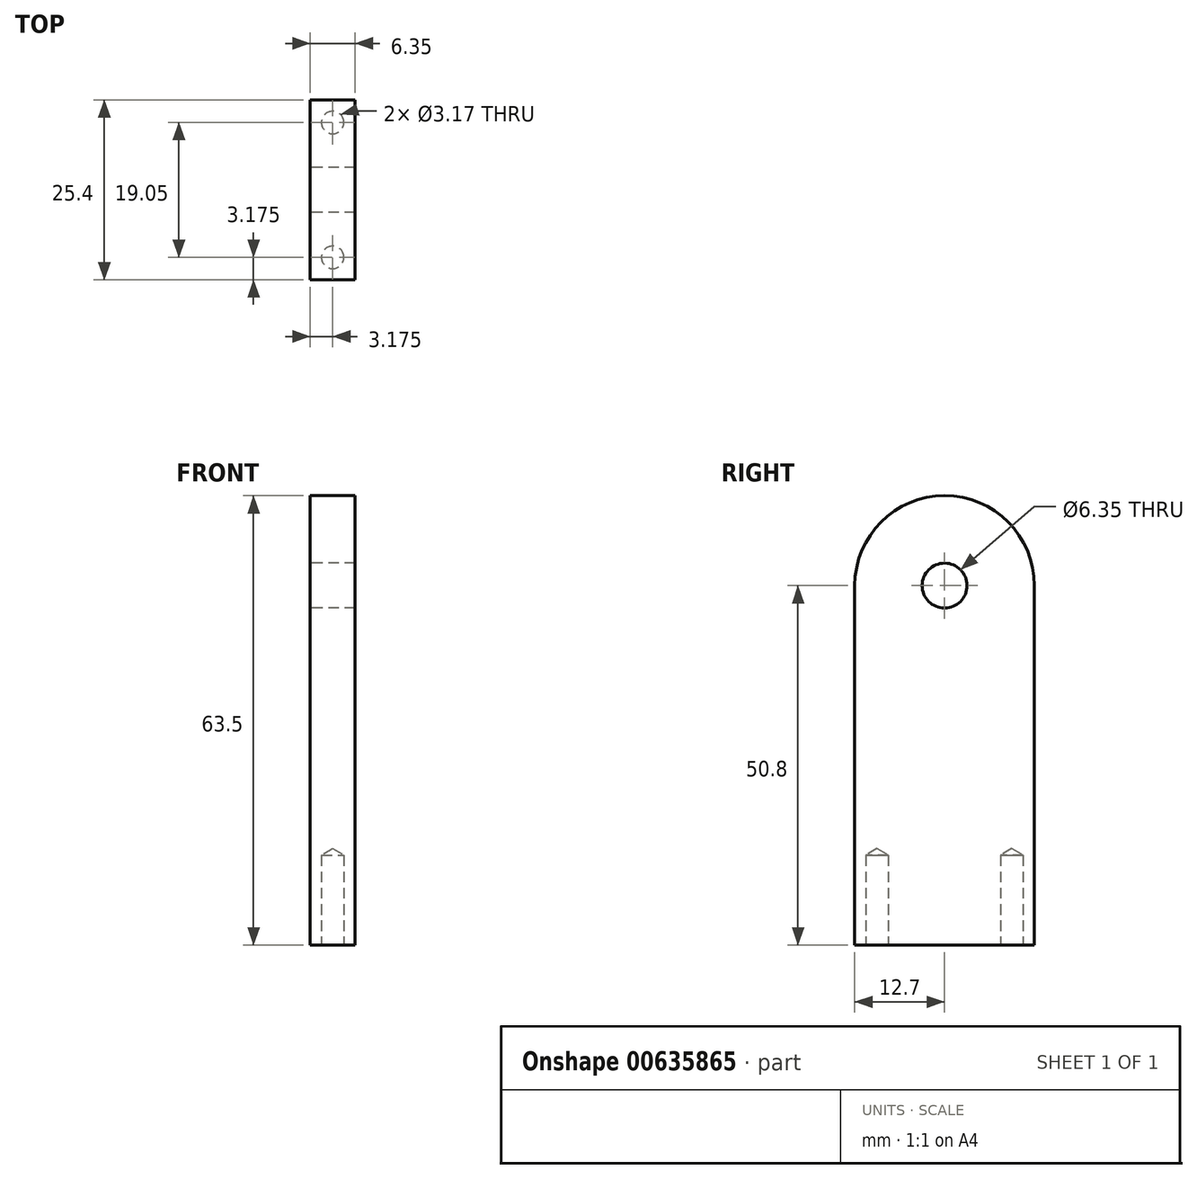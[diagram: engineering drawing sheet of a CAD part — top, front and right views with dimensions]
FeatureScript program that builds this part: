
annotation { "Feature Type Name" : "Feature", "Feature Type Description" : "" }
export const myFeature = defineFeature(function(context is Context, id is Id, definition is map)
    precondition{}
    {
        {
            var Q0;
            Q0=qCreatedBy(makeId("Right.planeOp"),FACE);
            var sketch = newSketch(context, id + "F0", { "sketchPlane" : qUnion([Q0])});
            skLineSegment(sketch, "E0.bottom", {"start": v(0, 0) * mm, "end": v(25.4, 0) * mm});
            skLineSegment(sketch, "E0.top", {"start": v(0, 50.8) * mm, "end": v(25.4, 50.8) * mm});
            skLineSegment(sketch, "E0.left", {"start": v(0, 0) * mm, "end": v(0, 50.8) * mm});
            skLineSegment(sketch, "E0.right", {"start": v(25.4, 0) * mm, "end": v(25.4, 50.8) * mm});
            skCircle(sketch, "E1", {"center": v(12.7, 50.8) * mm, "radius": 12.7 * mm});
            skCircle(sketch, "E2", {"center": v(12.7, 50.8) * mm, "radius": 3.18 * mm});
            skSolve(sketch);
        }
        {
            var Q0;
            Q0=makeQuery(id+"F0.imprint","IMPRINT",FACE,{"disambiguationData":[TD([[makeQuery(id+"F0.imprint","IMPRINT",EDGE,{"derivedFrom":sQuery(id+"F0.wireOp",EDGE,"E0.bottom")}),1.0]])]});
            var Q1;
            {var subQ1=sQuery(id+"F0.wireOp",EDGE,"E0.top");var subQ3=sQuery(id+"F0.wireOp",EDGE,"E2");var subQ4=makeQuery(id+"F0.imprint","INTERSECT",VERTEX,{"disambiguationData":[OD(0.0)],"derivedFrom":[subQ1,subQ3]});Q1=makeQuery(id+"F0.imprint","IMPRINT",FACE,{"disambiguationData":[TD([[makeQuery(id+"F0.imprint","IMPRINT",EDGE,{"disambiguationData":[TD([[subQ4,-1.0]])],"derivedFrom":subQ3}),-1.0]])]});}
            var Q2;
            {var subQ1=sQuery(id+"F0.wireOp",EDGE,"E0.top");var subQ3=sQuery(id+"F0.wireOp",EDGE,"E2");var subQ4=makeQuery(id+"F0.imprint","INTERSECT",VERTEX,{"disambiguationData":[OD(0.0)],"derivedFrom":[subQ1,subQ3]});Q2=makeQuery(id+"F0.imprint","IMPRINT",FACE,{"disambiguationData":[TD([[makeQuery(id+"F0.imprint","IMPRINT",EDGE,{"disambiguationData":[TD([[subQ4,1.0]])],"derivedFrom":subQ3}),-1.0]])]});}
            extrude(context, id + "F1", {"entities" : qUnion([Q0, Q1, Q2]), "depth" : 6.35 * mm, "offsetDistance" : 25.4 * mm});
        }
        {
            var Q0;
            Q0=makeQuery(id+"F1.opExtrude","SWEPT_FACE",FACE,{"disambiguationData":[OSD([sQuery(id+"F0.wireOp",EDGE,"E0.bottom")])]});
            var sketch = newSketch(context, id + "F2", { "sketchPlane" : qUnion([Q0])});
            skLineSegment(sketch, "E3", {"start": v(0, -3.18) * mm, "end": v(6.35, -3.17) * mm, "construction": true});
            skLineSegment(sketch, "E4", {"start": v(0, -22.22) * mm, "end": v(6.35, -22.22) * mm, "construction": true});
            skPoint(sketch, "E5", {"position": v(3.18, -3.17) * mm});
            skPoint(sketch, "E6", {"position": v(3.18, -22.22) * mm});
            skSolve(sketch);
        }
        {
            var Q0;
            Q0=sQuery(id+"F2.wireOp",VERTEX,"E5");
            var Q1;
            Q1=sQuery(id+"F2.wireOp",VERTEX,"E6");
            var Q2;
            Q2=makeQuery(id+"F1.opExtrude","SWEPT_BODY",BODY,{"disambiguationData":[OSD([sQuery(id+"F0.wireOp",EDGE,"E0.bottom"),sQuery(id+"F0.wireOp",EDGE,"E0.left"),sQuery(id+"F0.wireOp",EDGE,"E0.right"),sQuery(id+"F0.wireOp",EDGE,"E1"),sQuery(id+"F0.wireOp",EDGE,"E2")])]});
            hole(context, id + "F3", {"style" : HoleStyle.SIMPLE, "endStyle" : HoleEndStyle.BLIND, "holeDiameter" : 3.17 * mm, "majorDiameter" : 6.35 * mm, "holeDepth" : 12.7 * mm, "isTappedThrough" : true, "tappedDepth" : 12.7 * mm, "tapClearance" : 3, "locations" : qUnion([Q0, Q1]), "scope" : qUnion([Q2])});
        }
    });
